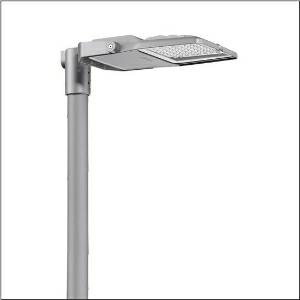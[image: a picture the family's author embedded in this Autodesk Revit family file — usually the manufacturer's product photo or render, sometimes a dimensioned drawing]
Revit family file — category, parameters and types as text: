
# Revit family: floodlight_fl_21_mini___pl52_5xa7775c2d3a_b3eb
name_source: partatom
category: Lighting Fixtures
units: mm (PartAtom-declared; Revit-internal decimal feet)

## family parameters
Cut with Voids When Loaded = No
Host = Face
Light Source = No
Part Type = Normal
Room Calculation Point = No
Round Connector Dimension = Use Diameter
Shared = No

## types (1)
- --- (1 x LED, 12190 lm, 89 W, 3000K)
    Apparent Load = 89 VA
    CIE Flux Codes = 26 60 98 100 100
    Color Rendering = 70
    Color Temperature = 3000K
    Default Elevation = 1800 mm
    Description = Floodlight FL 21 mini, floodlight, primary light control with lens, of PMMA, primary optical cover: protective disc, of toughened safety glass, transparent, light distribution: PL52, light emission: direct distribution, installation type: surface-mounted, LED, High Power LED, rated luminous flux: 12.190lm, luminous efficacy: 137lm/W, light colour: 730, colour temperature: 3000K, control gear: Smart Interface (Zhaga), control: flexible luminous flux parameterisation, time-dependent luminous flux control, constant luminous flux control, overheat protection, pre-setting: logarithmic dimming characteristic, with terminal, 6-pole, mains connection: 220..240V, AC, 50/60Hz, start of lifetime: 89W, end of service life: 94W, reduction: 43W, luminaire housing, of diecast aluminium, powder-coated, Siteco® metallic grey (DB 702S), corrosivity category C5 mid according to DIN EN ISO 12944, suitable for swimming pools, chlorine-resistant, sealing non-destructively replaceable, please order mast flange separately, mast bracket, of steel, galvanised, powder-coated, Siteco® metallic grey (DB 702S), Smart Interface above, protection rating (complete): IP66, insulation class (complete): insulation class II (safety insulation), certification: CE, ENEC, VDE, protection symbol: D, impact resistance: IK08, permissible operating ambient temperature: -40..+40°C, permissible operating ambient temperature for outdoor applications: -40..+50°C, standard: DIN EN 12944, LABS conformity tested according to VDMA 24364:2018-05, packaging unit: 1 piece

Light Distribution: PL52
    Height = 70 mm
    Lamp = 1 x LED
    Lamp Light Flux = 12190 lm
    Lamp Power = 89 W
    Lamp count = 1
    Length = 485 mm
    Luminous efficacy = 137 lm/W
    Manufacturer = Siteco
    ModVariant = No
    Model = 5XA7775C2D3A
    Number of Poles = 1
    OnlyDefault = Yes
    Power Factor = 1
    Product Name = Floodlight FL 21 mini | PL52
    Product group = floodlight | pylon annexe
    ProductGroupID = 6201
    Protection Class = Protection class II
    Protection Degree = IP 66
    RLX_Detail_Level = 1
    RLX_Emergency_Light_Flux = 0 lm
    RLX_Emergency_Type = 0
    RLX_Emergency_Type_DB = No
    RlxData = <blob elided: 101269 chars, md5=8f07a0f6>
    Socket = socket
    Standby Power = 0 W
    System Light Flux = 12190 lm
    System Power = 89 W
    Type Comments = factory setting: luminous flux: 100 % | dim-lin: 254 | 456 mA
    Type Image = l_1007125.jpg
    URL = http://relux.com
    VarID = @adj_184775
    Voltage = 0 V
    Weight = 0.00 kg
    Width = 337 mm

## geometry (parser evidence)
native form markers: Blend x4, Sweep x13
no freeform markers — native parametric forms only
